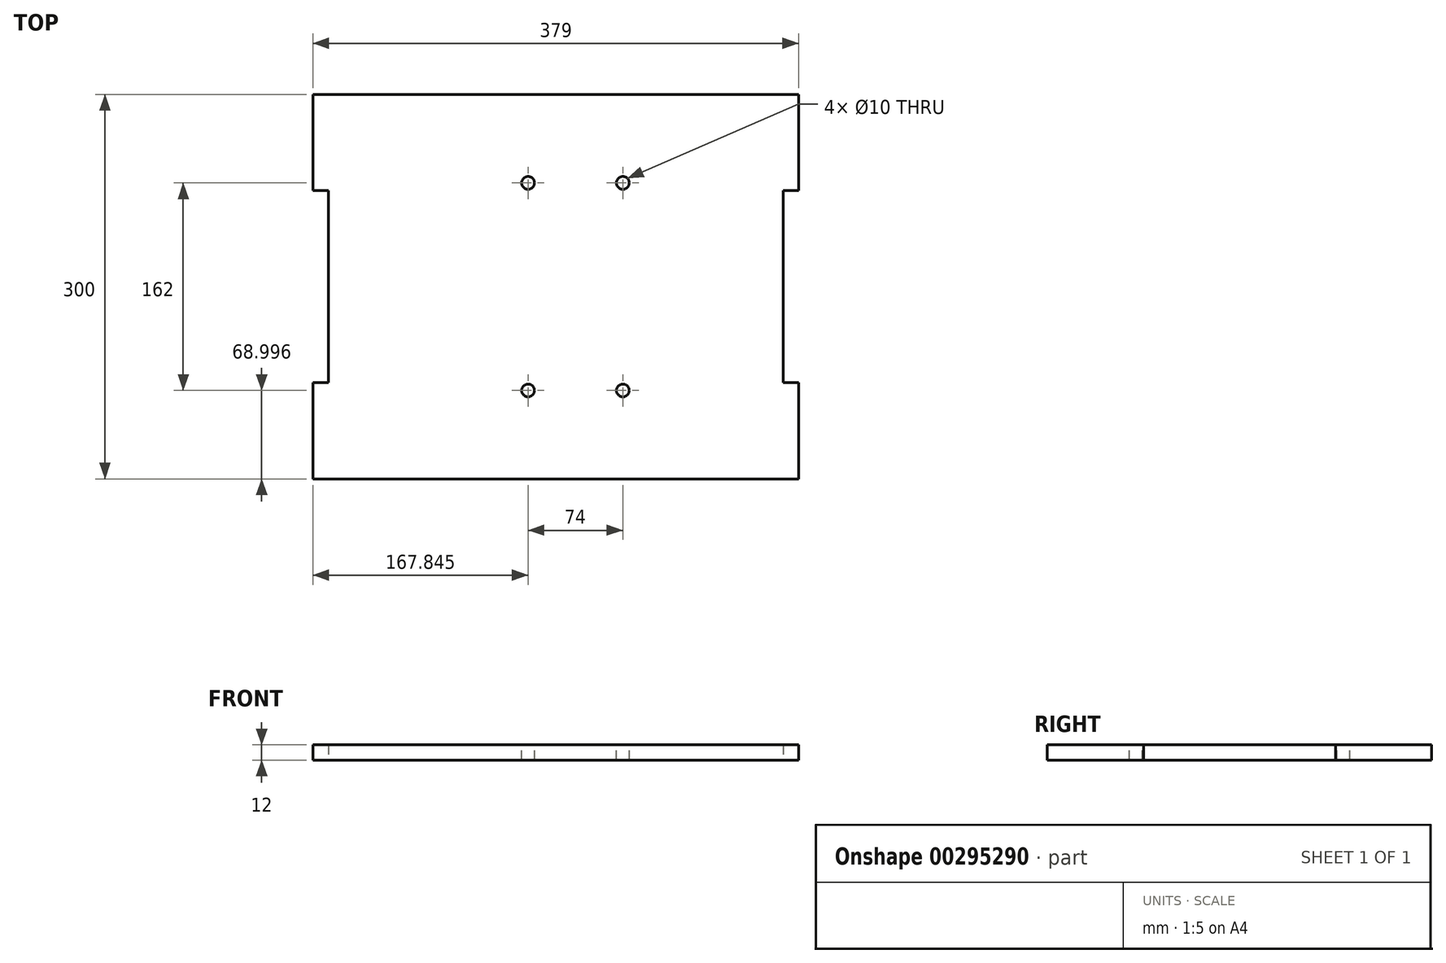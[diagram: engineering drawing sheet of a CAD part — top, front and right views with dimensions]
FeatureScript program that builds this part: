
annotation { "Feature Type Name" : "Feature", "Feature Type Description" : "" }
export const myFeature = defineFeature(function(context is Context, id is Id, definition is map)
    precondition{}
    {
        {
            var Q0;
            Q0=qCreatedBy(makeId("Top.planeOp"),FACE);
            var sketch = newSketch(context, id + "F0", { "sketchPlane" : qUnion([Q0])});
            skLineSegment(sketch, "E0", {"start": v(-217.36, 149.56) * mm, "end": v(161.64, 149.56) * mm});
            skLineSegment(sketch, "E1", {"start": v(161.64, 149.56) * mm, "end": v(161.64, 74.56) * mm});
            skLineSegment(sketch, "E2", {"start": v(149.64, 74.56) * mm, "end": v(149.64, -75.44) * mm});
            skLineSegment(sketch, "E3", {"start": v(149.64, -75.44) * mm, "end": v(161.64, -75.44) * mm});
            skLineSegment(sketch, "E4", {"start": v(161.64, -75.44) * mm, "end": v(161.64, -150.44) * mm});
            skLineSegment(sketch, "E5", {"start": v(161.64, -150.44) * mm, "end": v(-217.36, -150.44) * mm});
            skLineSegment(sketch, "E6", {"start": v(-217.36, -150.44) * mm, "end": v(-217.36, -75.44) * mm});
            skLineSegment(sketch, "E7", {"start": v(-217.36, -75.44) * mm, "end": v(-205.36, -75.44) * mm});
            skLineSegment(sketch, "E8", {"start": v(-205.36, -75.44) * mm, "end": v(-205.36, 74.56) * mm});
            skLineSegment(sketch, "E9", {"start": v(-205.36, 74.56) * mm, "end": v(-217.36, 74.56) * mm});
            skLineSegment(sketch, "E10", {"start": v(149.64, 74.56) * mm, "end": v(161.64, 74.56) * mm});
            skLineSegment(sketch, "E11", {"start": v(-217.36, 74.56) * mm, "end": v(-217.36, 149.56) * mm});
            skSolve(sketch);
        }
        {
            var Q0;
            Q0 = qSketchRegion(id + "F0", true);
            extrude(context, id + "F1", {"entities" : qUnion([Q0]), "depth" : 12 * mm});
        }
        {
            var Q0;
            Q0=makeQuery(id+"F1.opExtrude","CAP_FACE",FACE,{"disambiguationData":[OSD([sQuery(id+"F0.wireOp",EDGE,"E0"),sQuery(id+"F0.wireOp",EDGE,"E1"),sQuery(id+"F0.wireOp",EDGE,"E2"),sQuery(id+"F0.wireOp",EDGE,"E3"),sQuery(id+"F0.wireOp",EDGE,"E4"),sQuery(id+"F0.wireOp",EDGE,"E5"),sQuery(id+"F0.wireOp",EDGE,"E6"),sQuery(id+"F0.wireOp",EDGE,"E7"),sQuery(id+"F0.wireOp",EDGE,"E8"),sQuery(id+"F0.wireOp",EDGE,"E9"),sQuery(id+"F0.wireOp",EDGE,"E10"),sQuery(id+"F0.wireOp",EDGE,"E11")])],"isStart":false});
            var sketch = newSketch(context, id + "F2", { "sketchPlane" : qUnion([Q0])});
            skPoint(sketch, "E12", {"position": v(-49.51, 80.56) * mm});
            skPoint(sketch, "E13", {"position": v(24.49, 80.56) * mm});
            skPoint(sketch, "E14", {"position": v(24.49, -81.44) * mm});
            skPoint(sketch, "E15", {"position": v(-49.51, -81.44) * mm});
            skSolve(sketch);
        }
        {
            var Q0;
            Q0=sQuery(id+"F2.wireOp",VERTEX,"E12");
            var Q1;
            Q1=sQuery(id+"F2.wireOp",VERTEX,"E13");
            var Q2;
            Q2=sQuery(id+"F2.wireOp",VERTEX,"E14");
            var Q3;
            Q3=sQuery(id+"F2.wireOp",VERTEX,"E15");
            var Q4;
            Q4=makeQuery(id+"F1.opExtrude","SWEPT_BODY",BODY,{"disambiguationData":[OSD([sQuery(id+"F0.wireOp",EDGE,"E0"),sQuery(id+"F0.wireOp",EDGE,"E1"),sQuery(id+"F0.wireOp",EDGE,"E2"),sQuery(id+"F0.wireOp",EDGE,"E3"),sQuery(id+"F0.wireOp",EDGE,"E4"),sQuery(id+"F0.wireOp",EDGE,"E5"),sQuery(id+"F0.wireOp",EDGE,"E6"),sQuery(id+"F0.wireOp",EDGE,"E7"),sQuery(id+"F0.wireOp",EDGE,"E8"),sQuery(id+"F0.wireOp",EDGE,"E9"),sQuery(id+"F0.wireOp",EDGE,"E10"),sQuery(id+"F0.wireOp",EDGE,"E11")])]});
            hole(context, id + "F3", {"style" : HoleStyle.SIMPLE, "endStyle" : HoleEndStyle.THROUGH, "standardTappedOrClearance" : lookupTablePath({ "standard" : "ISO", "size" : "10", "type" : "Drilled" }), "standardBlindInLast" : lookupTablePath({ "standard" : "ISO", "size" : "10", "type" : "Drilled" }), "holeDiameter" : 10 * mm, "tappedDepth" : 12 * mm, "tapClearance" : 3, "locations" : qUnion([Q0, Q1, Q2, Q3]), "scope" : qUnion([Q4])});
        }
    });
